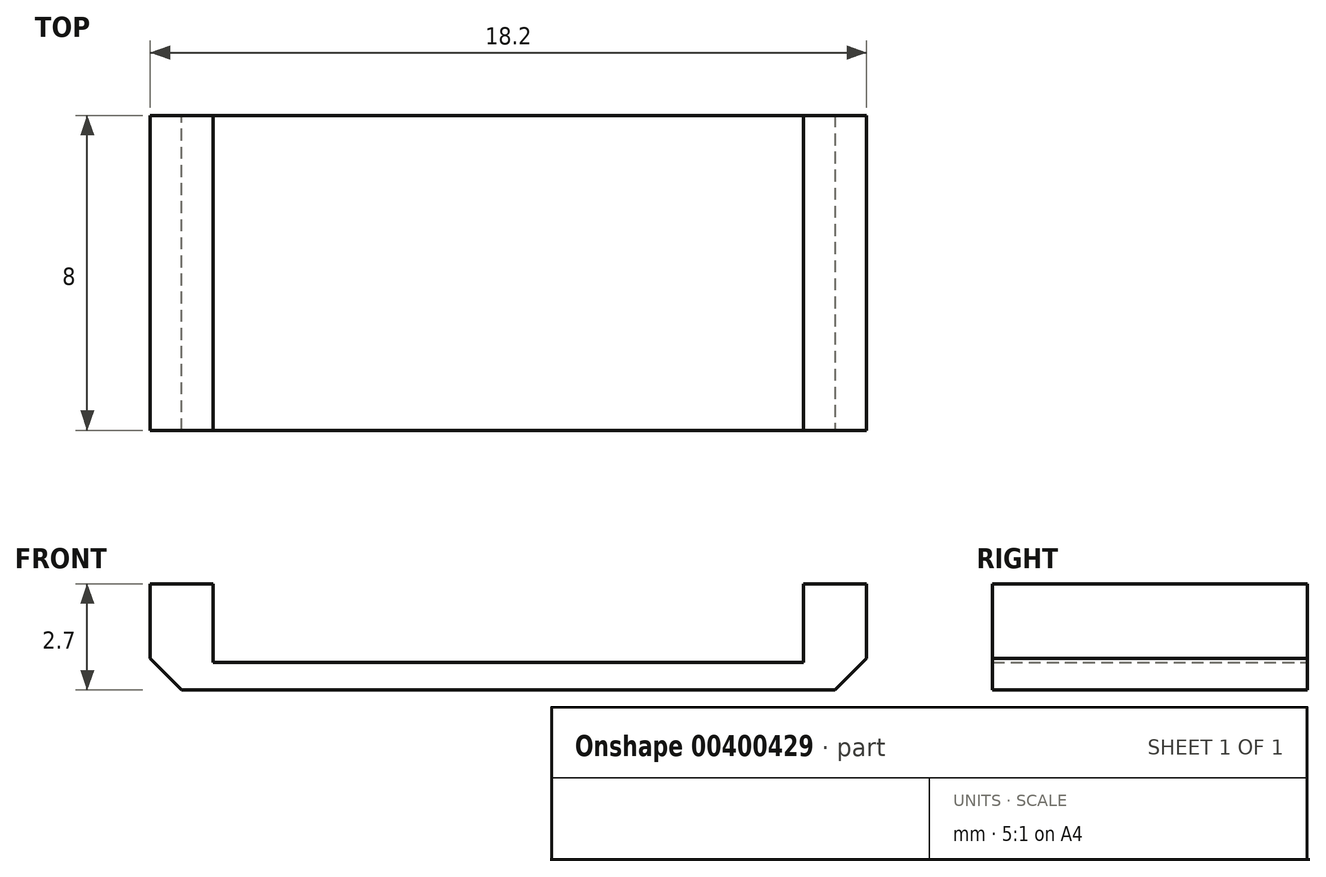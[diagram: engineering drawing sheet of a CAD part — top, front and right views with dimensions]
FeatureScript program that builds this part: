
annotation { "Feature Type Name" : "Feature", "Feature Type Description" : "" }
export const myFeature = defineFeature(function(context is Context, id is Id, definition is map)
    precondition{}
    {
        {
            var Q0;
            Q0=qCreatedBy(makeId("Top.planeOp"),FACE);
            var sketch = newSketch(context, id + "F0", { "sketchPlane" : qUnion([Q0])});
            skLineSegment(sketch, "E0.bottom", {"start": v(-9.1, 4) * mm, "end": v(9.1, 4) * mm});
            skLineSegment(sketch, "E0.top", {"start": v(-9.1, -4) * mm, "end": v(9.1, -4) * mm});
            skLineSegment(sketch, "E0.left", {"start": v(-9.1, 4) * mm, "end": v(-9.1, -4) * mm});
            skLineSegment(sketch, "E0.right", {"start": v(9.1, 4) * mm, "end": v(9.1, -4) * mm});
            skLineSegment(sketch, "E1", {"start": v(-9.1, -4) * mm, "end": v(9.1, 4) * mm, "construction": true});
            skSolve(sketch);
        }
        {
            var Q0;
            Q0=makeQuery(id+"F0.imprint","IMPRINT",FACE,{"disambiguationData":[TD([[makeQuery(id+"F0.imprint","IMPRINT",EDGE,{"derivedFrom":sQuery(id+"F0.wireOp",EDGE,"E0.bottom")}),-1.0]])]});
            extrude(context, id + "F1", {"entities" : qUnion([Q0]), "depth" : 2.7 * mm, "offsetDistance" : 25 * mm});
        }
        {
            var Q0;
            Q0=makeQuery(id+"F1.opExtrude","CAP_FACE",FACE,{"disambiguationData":[OSD([sQuery(id+"F0.wireOp",EDGE,"E0.bottom"),sQuery(id+"F0.wireOp",EDGE,"E0.top"),sQuery(id+"F0.wireOp",EDGE,"E0.left"),sQuery(id+"F0.wireOp",EDGE,"E0.right")])],"isStart":false});
            var sketch = newSketch(context, id + "F2", { "sketchPlane" : qUnion([Q0])});
            skLineSegment(sketch, "E2.bottom", {"start": v(-7.5, -4) * mm, "end": v(7.5, -4) * mm});
            skLineSegment(sketch, "E2.top", {"start": v(-7.5, 4) * mm, "end": v(7.5, 4) * mm});
            skLineSegment(sketch, "E2.left", {"start": v(-7.5, -4) * mm, "end": v(-7.5, 4) * mm});
            skLineSegment(sketch, "E2.right", {"start": v(7.5, -4) * mm, "end": v(7.5, 4) * mm});
            skLineSegment(sketch, "E3", {"start": v(-7.5, -4) * mm, "end": v(7.5, 4) * mm, "construction": true});
            skSolve(sketch);
        }
        {
            var Q0;
            Q0=makeQuery(id+"F2.imprint","IMPRINT",FACE,{"disambiguationData":[TD([[makeQuery(id+"F2.imprint","IMPRINT",EDGE,{"derivedFrom":sQuery(id+"F2.wireOp",EDGE,"E2.bottom")}),1.0]])]});
            extrude(context, id + "F3", {"entities" : qUnion([Q0]), "operationType" : NewBodyOperationType.REMOVE, "oppositeDirection" : true, "depth" : 2 * mm, "offsetDistance" : 25 * mm});
        }
        {
            var Q0;
            Q0=makeQuery(id+"F1.opExtrude","CAP_EDGE",EDGE,{"disambiguationData":[OSD([sQuery(id+"F0.wireOp",EDGE,"E0.left")])],"isStart":true});
            var Q1;
            Q1=makeQuery(id+"F1.opExtrude","CAP_EDGE",EDGE,{"disambiguationData":[OSD([sQuery(id+"F0.wireOp",EDGE,"E0.right")])],"isStart":true});
            chamfer(context, id + "F4", {"entities" : qUnion([Q0, Q1]), "width" : 0.8 * mm, "tangentPropagation" : true});
        }
    });
